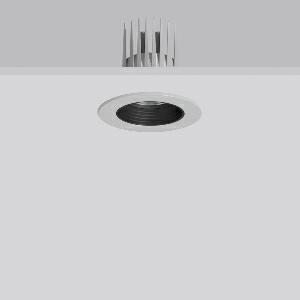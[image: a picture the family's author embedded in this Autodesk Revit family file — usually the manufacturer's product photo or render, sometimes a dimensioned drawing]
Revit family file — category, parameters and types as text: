
# Revit family: heledon_mini_e_901746_004_3_fb64
name_source: partatom
category: Lighting Fixtures
units: mm (PartAtom-declared; Revit-internal decimal feet)

## family parameters
Cut with Voids When Loaded = No
Host = Face
Light Source = No
Part Type = Normal
Room Calculation Point = No
Round Connector Dimension = Use Diameter
Shared = No

## types (1)
- HELEDON mini E (1 x LED Modul 935, 2300 lm, 3500)
    Apparent Load = 20 VA
    Approval mark = CE
    CIE Flux Codes = 80 99 100 100 100
    Color Rendering = 92
    Color Temperature = 3500
    Default Elevation = 1800 mm
    Description = Series: HELEDON mini
Round recessed downlight. Housing: die-cast aluminium, powder-coated. Black plastic ring and recessed LED to prevent glare from the side. Optical assembly with lens made of plastic (polycarbonate) for the best homogeneous light distribution - can be changed without tools. Best colour rendering index Ra>90. Suitable for Recessed ceiling mounting. Installation without tools thanks to spring fastening system. Including separate LED converter with connecting cable 600 mm.High quality converter without flickering and stroboscopic effect. Through-wiring box (5 pole) available as accessory. The following accessories can be mounted without use of tools: interchangeable lenses, decorative glasses, honeycomb louvre, clear and frosted diffusers, white interchangeable plastic ring. 
Colour: silver
Diameter: 124 mm
Height: 3 mm
Cut-out diameter: 114 mm
Recess height: 170 mm
Luminaire: recess height: 120 mm
Lamp: LED
Socket: without socket
Colour temperature: 3500K
Colour rendering index (CRI): 92
System power: 20 W
Rated luminous flux: 2300 lm
Luminous efficiency: 115 lm/W
Control gear: Regulated power supply
Protection class: II
Type of protection: IP 20
    Height = 0 mm  [stored 0 ft]
    Lamp = 1 x LED Modul 935
    Lamp Light Flux = 2300 lm
    Lamp count = 1
    Length = 124 mm  [stored 0.406824 ft]
    Lifetime = 50000 h
    Luminous efficacy = 115 lm/W
    Manufacturer = RZB
    ModVariant = No
    Model = 901746.004.3
    Mounting Place = Ceiling
    Mounting Type = Recessed
    Number of Poles = 1
    OnlyDefault = Yes
    Power Factor = 1
    Product Name = HELEDON mini E
    Product group = Recessed downlights
    ProductGroupID = 402
    Protection Class = Protection class II
    Protection Degree = IP 20
    RLX_Detail_Level = 1
    RLX_Emergency_Light_Flux = 0 lm
    RLX_Emergency_Type = 0
    RLX_Emergency_Type_DB = No
    RlxData = <blob elided: 125425 chars, md5=22ba5dde>
    Socket = socket
    Standby Power = 0 W
    System Light Flux = 2300 lm
    System Power = 20 W
    Type Comments = Product without accessories
    Type Image = 901656.004.jpg
    URL = http://relux.com
    VarID = ---
    Voltage = 230 V
    Voltage Range = 220-240 V
    Weight = 0.00 kg
    Width = 0 mm  [stored 0 ft]

note: [stored X ft] marks values corroborated as IEEE doubles in the binary element streams (Revit-internal decimal feet)

## geometry (parser evidence)
native form markers: Blend x4, Sweep x10
no freeform markers — native parametric forms only
